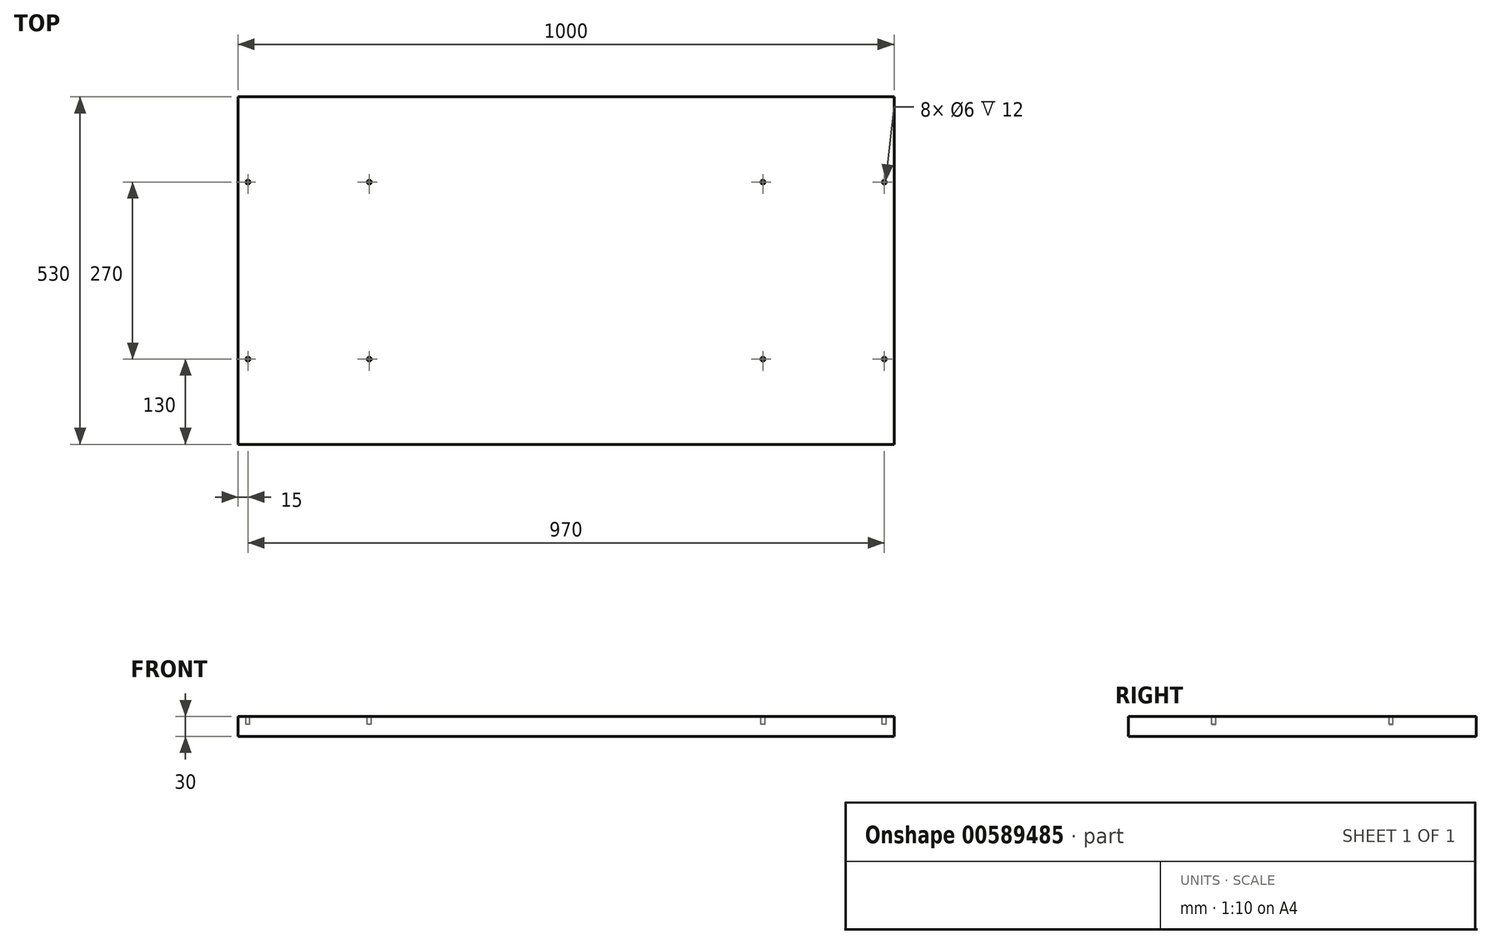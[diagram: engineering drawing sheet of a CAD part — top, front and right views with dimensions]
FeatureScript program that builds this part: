
annotation { "Feature Type Name" : "Feature", "Feature Type Description" : "" }
export const myFeature = defineFeature(function(context is Context, id is Id, definition is map)
    precondition{}
    {
        {
            var Q0;
            Q0=qCreatedBy(makeId("Top.planeOp"),FACE);
            var sketch = newSketch(context, id + "F0", { "sketchPlane" : qUnion([Q0])});
            skLineSegment(sketch, "E0.bottom", {"start": v(0, 0) * mm, "end": v(-1000, 0) * mm});
            skLineSegment(sketch, "E0.top", {"start": v(0, 530) * mm, "end": v(-1000, 530) * mm});
            skLineSegment(sketch, "E0.left", {"start": v(0, 0) * mm, "end": v(0, 530) * mm});
            skLineSegment(sketch, "E0.right", {"start": v(-1000, 0) * mm, "end": v(-1000, 530) * mm});
            skSolve(sketch);
        }
        {
            var Q0;
            Q0=qSketchRegion(id+"F0",true);
            extrude(context, id + "F1", {"entities" : qUnion([Q0]), "depth" : 30 * mm, "offsetDistance" : 25 * mm});
        }
        {
            var Q0;
            Q0=makeQuery(id+"F1.opExtrude","CAP_FACE",FACE,{"disambiguationData":[OSD([sQuery(id+"F0.wireOp",EDGE,"E0.bottom"),sQuery(id+"F0.wireOp",EDGE,"E0.top"),sQuery(id+"F0.wireOp",EDGE,"E0.left"),sQuery(id+"F0.wireOp",EDGE,"E0.right")])],"isStart":false});
            var sketch = newSketch(context, id + "F2", { "sketchPlane" : qUnion([Q0])});
            skCircle(sketch, "E1", {"center": v(-200, 130) * mm, "radius": 3 * mm});
            skSolve(sketch);
        }
        {
            var Q0;
            Q0=makeQuery(id+"F2.imprint","IMPRINT",FACE,{"disambiguationData":[TD([[makeQuery(id+"F2.imprint","IMPRINT",EDGE,{"derivedFrom":sQuery(id+"F2.wireOp",EDGE,"E1")}),1.0]])]});
            extrude(context, id + "F3", {"entities" : qUnion([Q0]), "operationType" : NewBodyOperationType.REMOVE, "oppositeDirection" : true, "depth" : 12 * mm, "offsetDistance" : 25 * mm});
        }
        {
            var Q0;
            Q0=makeQuery(id+"F1.opExtrude","CAP_FACE",FACE,{"disambiguationData":[OSD([sQuery(id+"F0.wireOp",EDGE,"E0.bottom"),sQuery(id+"F0.wireOp",EDGE,"E0.top"),sQuery(id+"F0.wireOp",EDGE,"E0.left"),sQuery(id+"F0.wireOp",EDGE,"E0.right")])],"isStart":false});
            var sketch = newSketch(context, id + "F4", { "sketchPlane" : qUnion([Q0])});
            skCircle(sketch, "E2", {"center": v(-800, 130) * mm, "radius": 3 * mm});
            skSolve(sketch);
        }
        {
            var Q0;
            Q0=makeQuery(id+"F4.imprint","IMPRINT",FACE,{"disambiguationData":[TD([[makeQuery(id+"F4.imprint","IMPRINT",EDGE,{"derivedFrom":sQuery(id+"F4.wireOp",EDGE,"E2")}),1.0]])]});
            extrude(context, id + "F5", {"entities" : qUnion([Q0]), "operationType" : NewBodyOperationType.REMOVE, "oppositeDirection" : true, "depth" : 12 * mm, "offsetDistance" : 25 * mm});
        }
        {
            var Q0;
            Q0=makeQuery(id+"F1.opExtrude","CAP_FACE",FACE,{"disambiguationData":[OSD([sQuery(id+"F0.wireOp",EDGE,"E0.bottom"),sQuery(id+"F0.wireOp",EDGE,"E0.top"),sQuery(id+"F0.wireOp",EDGE,"E0.left"),sQuery(id+"F0.wireOp",EDGE,"E0.right")])],"isStart":false});
            var sketch = newSketch(context, id + "F6", { "sketchPlane" : qUnion([Q0])});
            skCircle(sketch, "E3", {"center": v(-800, 400) * mm, "radius": 3 * mm});
            skCircle(sketch, "E4", {"center": v(-200, 400) * mm, "radius": 3 * mm});
            skSolve(sketch);
        }
        {
            var Q0;
            Q0=makeQuery(id+"F6.imprint","IMPRINT",FACE,{"disambiguationData":[TD([[makeQuery(id+"F6.imprint","IMPRINT",EDGE,{"derivedFrom":sQuery(id+"F6.wireOp",EDGE,"E4")}),1.0]])]});
            var Q1;
            Q1=makeQuery(id+"F6.imprint","IMPRINT",FACE,{"disambiguationData":[TD([[makeQuery(id+"F6.imprint","IMPRINT",EDGE,{"derivedFrom":sQuery(id+"F6.wireOp",EDGE,"E3")}),1.0]])]});
            extrude(context, id + "F7", {"entities" : qUnion([Q0, Q1]), "operationType" : NewBodyOperationType.REMOVE, "oppositeDirection" : true, "depth" : 12 * mm, "offsetDistance" : 25 * mm});
        }
        {
            var Q0;
            Q0=makeQuery(id+"F1.opExtrude","CAP_FACE",FACE,{"disambiguationData":[OSD([sQuery(id+"F0.wireOp",EDGE,"E0.bottom"),sQuery(id+"F0.wireOp",EDGE,"E0.top"),sQuery(id+"F0.wireOp",EDGE,"E0.left"),sQuery(id+"F0.wireOp",EDGE,"E0.right")])],"isStart":false});
            var sketch = newSketch(context, id + "F8", { "sketchPlane" : qUnion([Q0])});
            skCircle(sketch, "E5", {"center": v(-985, 400) * mm, "radius": 3 * mm});
            skSolve(sketch);
        }
        {
            var Q0;
            Q0=makeQuery(id+"F8.imprint","IMPRINT",FACE,{"disambiguationData":[TD([[makeQuery(id+"F8.imprint","IMPRINT",EDGE,{"derivedFrom":sQuery(id+"F8.wireOp",EDGE,"E5")}),-1.0]])]});
            var sketch = newSketch(context, id + "F9", { "sketchPlane" : qUnion([Q0])});
            skCircle(sketch, "E6", {"center": v(-985, 130) * mm, "radius": 3 * mm});
            skSolve(sketch);
        }
        {
            var Q0;
            Q0=makeQuery(id+"F9.imprint","IMPRINT",FACE,{"disambiguationData":[TD([[makeQuery(id+"F9.imprint","IMPRINT",EDGE,{"derivedFrom":sQuery(id+"F9.wireOp",EDGE,"E6")}),1.0]])]});
            var Q1;
            Q1=makeQuery(id+"F8.imprint","IMPRINT",FACE,{"disambiguationData":[TD([[makeQuery(id+"F8.imprint","IMPRINT",EDGE,{"derivedFrom":sQuery(id+"F8.wireOp",EDGE,"E5")}),1.0]])]});
            extrude(context, id + "F10", {"entities" : qUnion([Q0, Q1]), "operationType" : NewBodyOperationType.REMOVE, "oppositeDirection" : true, "depth" : 12 * mm, "offsetDistance" : 25 * mm});
        }
        {
            var Q0;
            Q0=makeQuery(id+"F1.opExtrude","CAP_FACE",FACE,{"disambiguationData":[OSD([sQuery(id+"F0.wireOp",EDGE,"E0.bottom"),sQuery(id+"F0.wireOp",EDGE,"E0.top"),sQuery(id+"F0.wireOp",EDGE,"E0.left"),sQuery(id+"F0.wireOp",EDGE,"E0.right")])],"isStart":false});
            var sketch = newSketch(context, id + "F11", { "sketchPlane" : qUnion([Q0])});
            skCircle(sketch, "E7", {"center": v(-15, 400) * mm, "radius": 3 * mm});
            skCircle(sketch, "E8", {"center": v(-15, 130) * mm, "radius": 3 * mm});
            skSolve(sketch);
        }
        {
            var Q0;
            Q0=makeQuery(id+"F11.imprint","IMPRINT",FACE,{"disambiguationData":[TD([[makeQuery(id+"F11.imprint","IMPRINT",EDGE,{"derivedFrom":sQuery(id+"F11.wireOp",EDGE,"E7")}),1.0]])]});
            var Q1;
            Q1=makeQuery(id+"F11.imprint","IMPRINT",FACE,{"disambiguationData":[TD([[makeQuery(id+"F11.imprint","IMPRINT",EDGE,{"derivedFrom":sQuery(id+"F11.wireOp",EDGE,"E8")}),1.0]])]});
            extrude(context, id + "F12", {"entities" : qUnion([Q0, Q1]), "operationType" : NewBodyOperationType.REMOVE, "oppositeDirection" : true, "depth" : 12 * mm, "offsetDistance" : 25 * mm});
        }
    });
